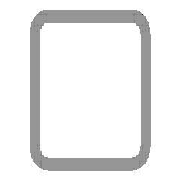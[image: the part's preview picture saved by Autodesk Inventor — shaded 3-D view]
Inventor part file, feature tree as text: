
AUTODESK INVENTOR PART (.ipt)
format: ipt  version: 2016 (Build 200138000, 138)  size: 148,992 bytes
history: native  units: mm (DEFAULTED — no unit token found)
features: other x5, sketch x2, sweep x1, plane x1
ambient origin geometry x8: Origin, YZ Plane, XZ Plane, XY Plane, X Axis, Y Axis, Z Axis, Center Point
bodies: Solid1 (feature_tree), Body (feature_tree)
feature tree (9):
  parser-record x1  (decoder bookkeeping rows leaked as tree rows — omitted from the tree; the rows remain in map.json)
  other  "Driven Length"
  other  "Start plane"
  other  "End plane"
  sweep  "Sweep Path"
  other  "Orientation Work Plane"
  sketch  "Sketch3"  dims[d7=4.0mm d9=60.0mm]
  plane  "Work Plane3"
  sketch  "Sketch4"  dims[d11=60.0mm d12=2.0mm d13=-0.0mm d14=306.305284mm d15=30.0mm d16=30.0mm d17=90.0deg d18=306.305284mm d19=0.0mm d20=0.0mm]
